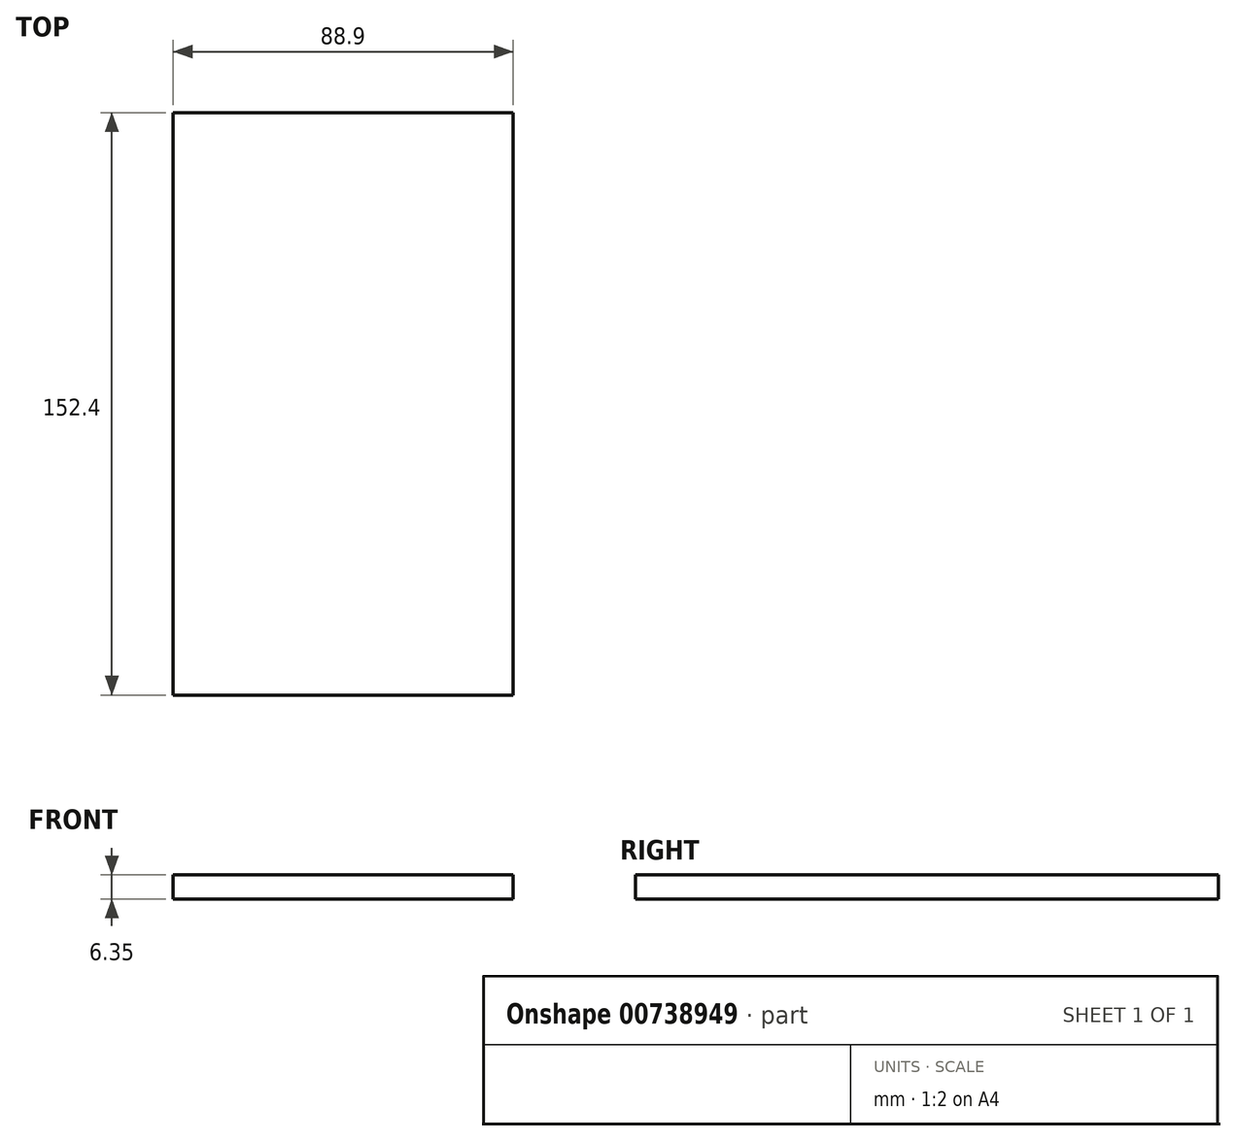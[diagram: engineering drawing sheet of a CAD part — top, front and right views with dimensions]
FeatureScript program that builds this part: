
annotation { "Feature Type Name" : "Feature", "Feature Type Description" : "" }
export const myFeature = defineFeature(function(context is Context, id is Id, definition is map)
    precondition{}
    {
        {
            var Q0;
            Q0=qCreatedBy(makeId("Top.planeOp"),FACE);
            var sketch = newSketch(context, id + "F0", { "sketchPlane" : qUnion([Q0])});
            skLineSegment(sketch, "E0.bottom", {"start": v(44.45, -76.2) * mm, "end": v(-44.45, -76.2) * mm});
            skLineSegment(sketch, "E0.top", {"start": v(44.45, 76.2) * mm, "end": v(-44.45, 76.2) * mm});
            skLineSegment(sketch, "E0.left", {"start": v(44.45, -76.2) * mm, "end": v(44.45, 76.2) * mm});
            skLineSegment(sketch, "E0.right", {"start": v(-44.45, -76.2) * mm, "end": v(-44.45, 76.2) * mm});
            skPoint(sketch, "E0.middle", {"position": v(0, 0) * mm});
            skSolve(sketch);
        }
        {
            var Q0;
            Q0=makeQuery(id+"F0.imprint","IMPRINT",FACE,{"disambiguationData":[TD([[makeQuery(id+"F0.imprint","IMPRINT",EDGE,{"derivedFrom":sQuery(id+"F0.wireOp",EDGE,"E0.bottom")}),-1.0]])]});
            extrude(context, id + "F1", {"entities" : qUnion([Q0]), "depth" : 6.35 * mm, "offsetDistance" : 25.4 * mm});
        }
    });
